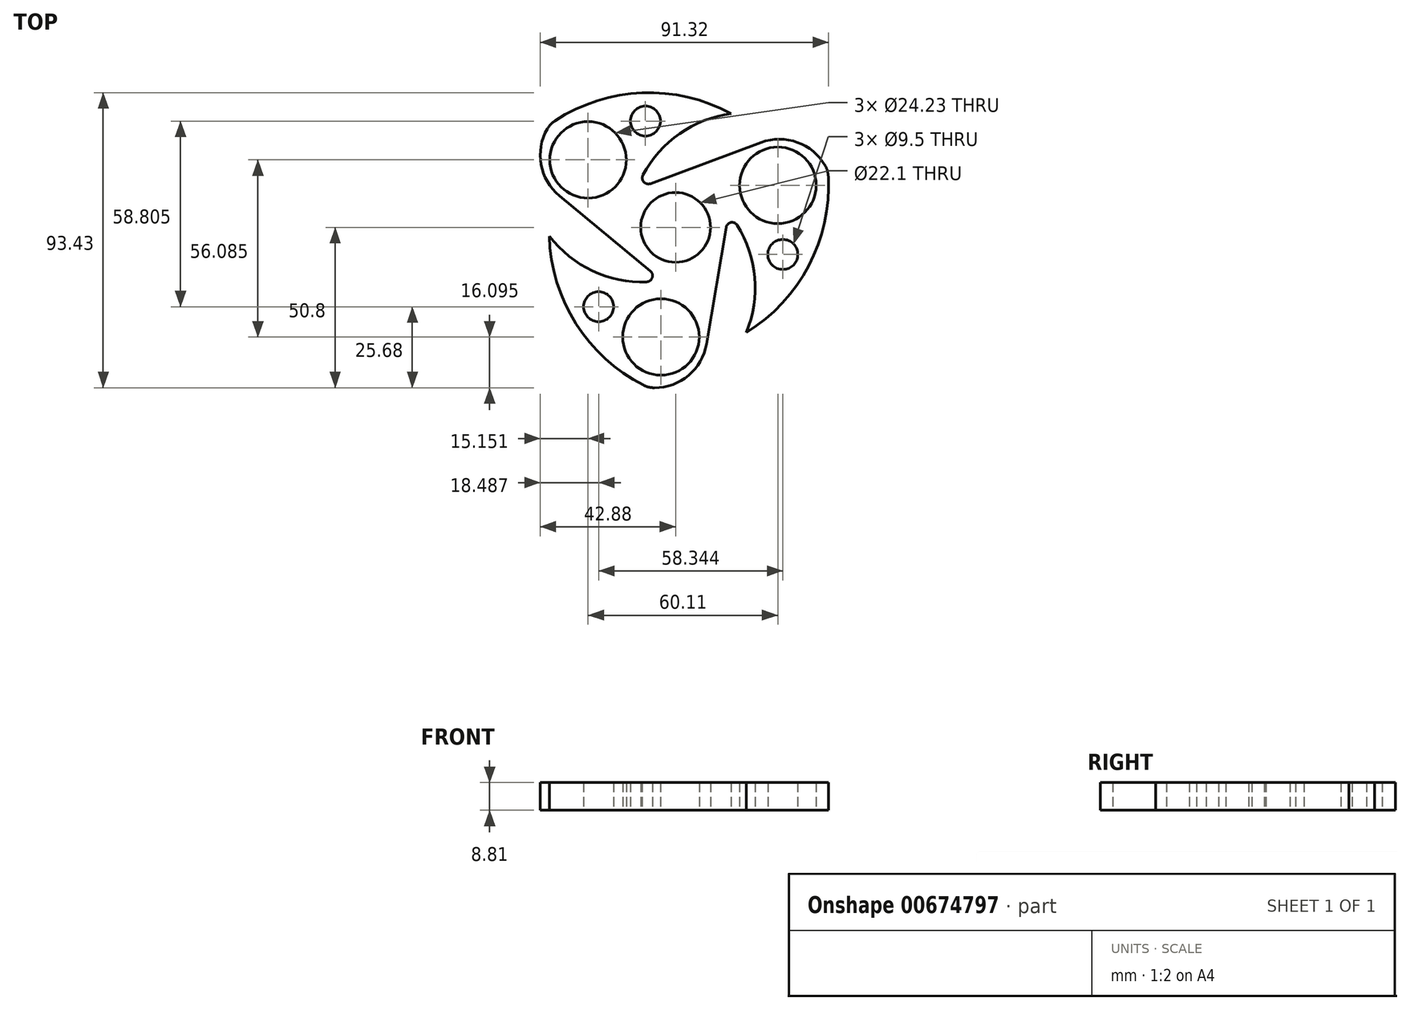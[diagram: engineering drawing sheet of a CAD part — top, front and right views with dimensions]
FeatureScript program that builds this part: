
annotation { "Feature Type Name" : "Feature", "Feature Type Description" : "" }
export const myFeature = defineFeature(function(context is Context, id is Id, definition is map)
    precondition{}
    {
        {
            var Q0;
            Q0=qCreatedBy(makeId("Top.planeOp"),FACE);
            var sketch = newSketch(context, id + "F0", { "sketchPlane" : qUnion([Q0])});
            skCircle(sketch, "E0", {"center": v(0, 0) * mm, "radius": 11.05 * mm});
            skCircle(sketch, "E1", {"center": v(32.38, 13.32) * mm, "radius": 12.12 * mm});
            skArc(sketch, "E2", {"start": v(48.25, 17.76) * mm, "mid": v(39.5, 26.58) * mm, "end": v(27.07, 26.9) * mm});
            skArc(sketch, "E3", {"start": v(22.42, -33.26) * mm, "mid": v(42.55, -11.4) * mm, "end": v(48.25, 17.76) * mm});
            skArc(sketch, "E4", {"start": v(22.42, -33.26) * mm, "mid": v(25.07, -15.93) * mm, "end": v(19.5, 0.7) * mm});
            skArc(sketch, "E5", {"start": v(19.5, 0.7) * mm, "mid": v(17.51, 1.56) * mm, "end": v(16, 0) * mm});
            skLineSegment(sketch, "E6", {"start": v(16, 0) * mm, "end": v(9.76, -36.9) * mm});
            skPoint(sketch, "E7.end.orphan", {"position": v(-12.23, -19.13) * mm});
            skPoint(sketch, "E7.start.orphan", {"position": v(-41.2, -7.33) * mm});
            skPoint(sketch, "E8.end.orphan", {"position": v(-6.54, -14.5) * mm});
            skPoint(sketch, "E9.start.orphan", {"position": v(12.91, 38.24) * mm});
            skPoint(sketch, "E10.start.orphan", {"position": v(-13.07, 14.39) * mm});
            skPoint(sketch, "E11.start.orphan", {"position": v(-10.34, 12.08) * mm});
            skPoint(sketch, "E12.center.orphan", {"position": v(-4.84, -34.68) * mm});
            skPoint(sketch, "E13.center.orphan", {"position": v(-27.73, 21.38) * mm});
            skCircle(sketch, "E14.1.1", {"center": v(-27.73, 21.38) * mm, "radius": 12.12 * mm});
            skArc(sketch, "E14.1.2", {"start": v(-39.5, 32.9) * mm, "mid": v(-42.76, 20.91) * mm, "end": v(-36.83, 10) * mm});
            skArc(sketch, "E14.1.3", {"start": v(17.6, 36.05) * mm, "mid": v(-11.4, 42.55) * mm, "end": v(-39.5, 32.9) * mm});
            skArc(sketch, "E14.1.4", {"start": v(17.6, 36.05) * mm, "mid": v(1.26, 29.67) * mm, "end": v(-10.36, 16.54) * mm});
            skArc(sketch, "E14.1.5", {"start": v(-10.36, 16.54) * mm, "mid": v(-10.1, 14.39) * mm, "end": v(-8, 13.86) * mm});
            skLineSegment(sketch, "E14.1.6", {"start": v(-8, 13.86) * mm, "end": v(27.07, 26.9) * mm});
            skCircle(sketch, "E14.2.1", {"center": v(-4.65, -34.7) * mm, "radius": 12.12 * mm});
            skArc(sketch, "E14.2.2", {"start": v(-8.74, -50.67) * mm, "mid": v(3.27, -47.5) * mm, "end": v(9.76, -36.9) * mm});
            skArc(sketch, "E14.2.3", {"start": v(-40.02, -2.8) * mm, "mid": v(-31.15, -31.15) * mm, "end": v(-8.74, -50.67) * mm});
            skArc(sketch, "E14.2.4", {"start": v(-40.02, -2.8) * mm, "mid": v(-26.33, -13.74) * mm, "end": v(-9.15, -17.24) * mm});
            skArc(sketch, "E14.2.5", {"start": v(-9.15, -17.24) * mm, "mid": v(-7.4, -15.95) * mm, "end": v(-8, -13.86) * mm});
            skLineSegment(sketch, "E14.2.6", {"start": v(-8, -13.86) * mm, "end": v(-36.83, 10) * mm});
            skCircle(sketch, "E15", {"center": v(-9.56, 33.69) * mm, "radius": 4.75 * mm});
            skCircle(sketch, "E16.1.0", {"center": v(-24.4, -25.12) * mm, "radius": 4.75 * mm});
            skCircle(sketch, "E16.2.0", {"center": v(33.95, -8.56) * mm, "radius": 4.75 * mm});
            skSolve(sketch);
        }
        {
            var Q0;
            Q0=makeQuery(id+"F0.imprint","IMPRINT",FACE,{"disambiguationData":[TD([[makeQuery(id+"F0.imprint","IMPRINT",EDGE,{"derivedFrom":sQuery(id+"F0.wireOp",EDGE,"E0")}),-1.0]])]});
            extrude(context, id + "F1", {"entities" : qUnion([Q0]), "depth" : 8.8 * mm, "offsetDistance" : 25.4 * mm});
        }
        {
            var Q0;
            Q0=makeQuery(id+"F1.opExtrude","SWEPT_EDGE",EDGE,{"disambiguationData":[OSD([sQuery(id+"F0.wireOp",EDGE,"E14.1.2"),sQuery(id+"F0.wireOp",EDGE,"E14.1.3")])]});
            var Q1;
            Q1=makeQuery(id+"F1.opExtrude","SWEPT_EDGE",EDGE,{"disambiguationData":[OSD([sQuery(id+"F0.wireOp",EDGE,"E2"),sQuery(id+"F0.wireOp",EDGE,"E3")])]});
            var Q2;
            Q2=makeQuery(id+"F1.opExtrude","SWEPT_EDGE",EDGE,{"disambiguationData":[OSD([sQuery(id+"F0.wireOp",EDGE,"E14.2.2"),sQuery(id+"F0.wireOp",EDGE,"E14.2.3")])]});
            fillet(context, id + "F2", {"entities" : qUnion([Q0, Q1, Q2]), "radius" : 7.62 * mm, "tangentPropagation" : true, "allowEdgeOverflow" : false});
        }
    });
